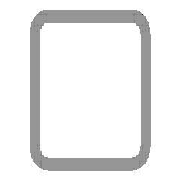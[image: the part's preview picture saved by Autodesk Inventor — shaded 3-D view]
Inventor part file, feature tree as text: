
AUTODESK INVENTOR PART (.ipt)
format: ipt  version: 2025.1 (Build 291241020, 241B)  size: 133,632 bytes
history: native  units: mm (DEFAULTED — no unit token found)
features: other x4, sketch x1, plane x1
ambient origin geometry x8: Origin, YZ Plane, XZ Plane, XY Plane, X Axis, Y Axis, Z Axis, Center Point
bodies: Solid1 (feature_tree), Body (feature_tree)
feature tree (6):
  parser-record x1  (decoder bookkeeping rows leaked as tree rows — omitted from the tree; the rows remain in map.json)
  other  "Driven Length"
  other  "Start Plane"
  other  "End Plane"
  sketch  "Sketch3"  dims[d3=1400.0mm d4=0.0mm d7=4.0mm d9=40.0mm d11=40.0mm d12=2.0mm d13=50.0mm d14=1450.0mm d15=20.0mm d16=20.0mm d17=90.0deg d18=1400.0mm]
  plane  "Work Plane3"
